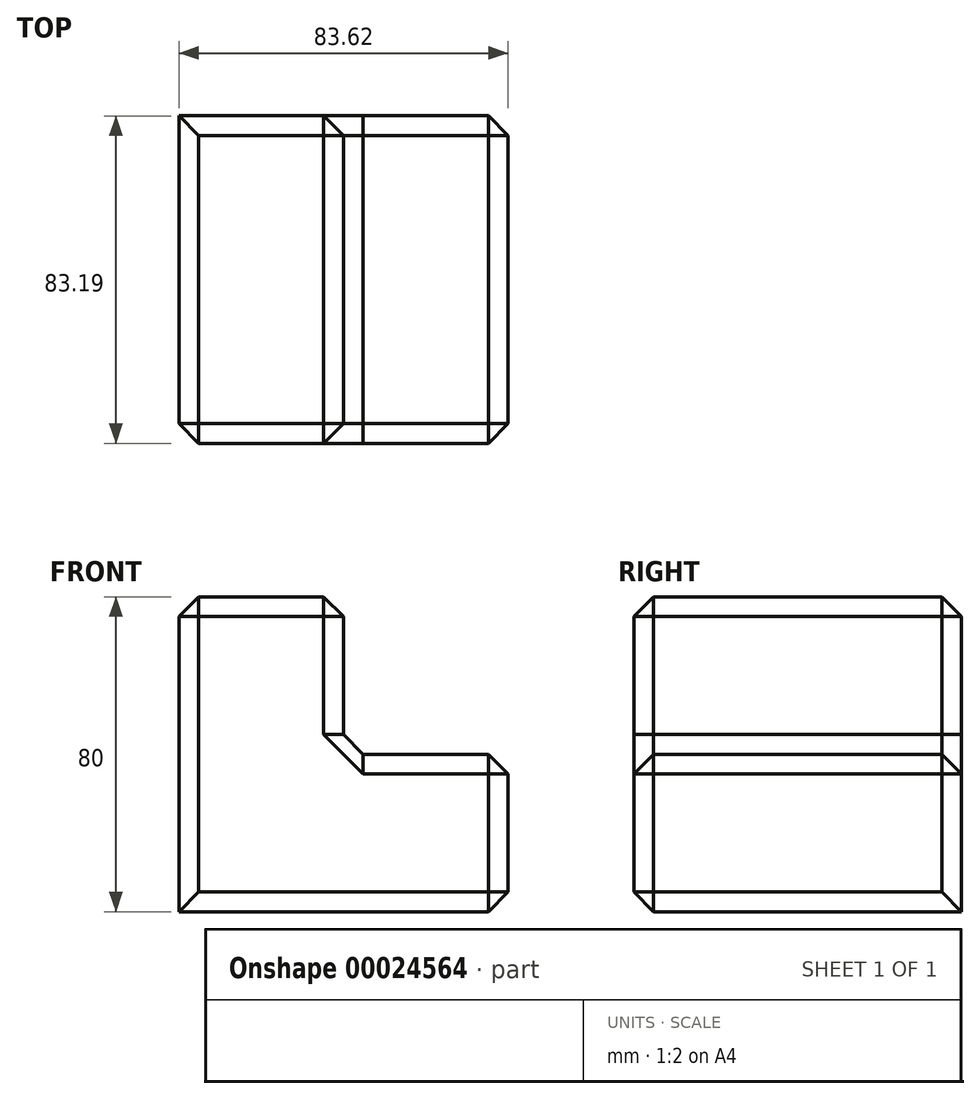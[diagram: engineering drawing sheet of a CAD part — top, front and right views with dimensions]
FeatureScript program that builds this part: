
annotation { "Feature Type Name" : "Feature", "Feature Type Description" : "" }
export const myFeature = defineFeature(function(context is Context, id is Id, definition is map)
    precondition{}
    {
        {
            var Q0;
            Q0=qCreatedBy(makeId("Top.planeOp"),FACE);
            var sketch = newSketch(context, id + "F0", { "sketchPlane" : qUnion([Q0])});
            skLineSegment(sketch, "E0.bottom", {"start": v(-59.13, -45.93) * mm, "end": v(24.5, -45.93) * mm});
            skLineSegment(sketch, "E0.top", {"start": v(-59.13, 37.26) * mm, "end": v(24.5, 37.26) * mm});
            skLineSegment(sketch, "E0.left", {"start": v(-59.13, -45.93) * mm, "end": v(-59.13, 37.26) * mm});
            skLineSegment(sketch, "E0.right", {"start": v(24.5, -45.93) * mm, "end": v(24.5, 37.26) * mm});
            skSolve(sketch);
        }
        {
            var Q0;
            Q0=makeQuery(id+"F0.imprint","IMPRINT",FACE,{"disambiguationData":[TD([[makeQuery(id+"F0.imprint","IMPRINT",EDGE,{"derivedFrom":sQuery(id+"F0.wireOp",EDGE,"E0.bottom")}),1.0]])]});
            extrude(context, id + "F1", {"entities" : qUnion([Q0]), "depth" : 40 * mm});
        }
        {
            var Q0;
            Q0=makeQuery(id+"F1.opExtrude","CAP_FACE",FACE,{"disambiguationData":[OSD([sQuery(id+"F0.wireOp",EDGE,"E0.bottom"),sQuery(id+"F0.wireOp",EDGE,"E0.top"),sQuery(id+"F0.wireOp",EDGE,"E0.left"),sQuery(id+"F0.wireOp",EDGE,"E0.right")])],"isStart":false});
            var sketch = newSketch(context, id + "F2", { "sketchPlane" : qUnion([Q0])});
            skLineSegment(sketch, "E1", {"start": v(-17.32, 37.26) * mm, "end": v(-17.32, -45.93) * mm});
            skSolve(sketch);
        }
        {
            var Q0;
            {var subQ1=sQuery(id+"F2.wireOp",EDGE,"E1");Q0=makeQuery(id+"F2.imprint","IMPRINT",FACE,{"disambiguationData":[TD([[makeQuery(id+"F2.imprint","IMPRINT",EDGE,{"derivedFrom":subQ1}),-1.0]])]});}
            extrude(context, id + "F3", {"entities" : qUnion([Q0]), "operationType" : NewBodyOperationType.ADD, "depth" : 40 * mm});
        }
        {
            var Q0;
            Q0=makeQuery(id+"F3.opExtrude","CAP_FACE",FACE,{"disambiguationData":[OSD([sQuery(id+"F0.wireOp",EDGE,"E0.bottom"),sQuery(id+"F0.wireOp",EDGE,"E0.top"),sQuery(id+"F0.wireOp",EDGE,"E0.left"),sQuery(id+"F2.wireOp",EDGE,"E1")])],"isStart":false});
            var Q1;
            {var subQ0=sQuery(id+"F0.wireOp",EDGE,"E0.bottom");Q1=makeQuery(id+"F3.boolean.opBoolean","MERGE",FACE,{"derivedFrom":[makeQuery(id+"F1.opExtrude","SWEPT_FACE",FACE,{"disambiguationData":[OSD([subQ0])]}),makeQuery(id+"F3.opExtrude","SWEPT_FACE",FACE,{"disambiguationData":[OSD([subQ0])]})]});}
            var Q2;
            Q2=makeQuery(id+"F1.opExtrude","CAP_FACE",FACE,{"disambiguationData":[OSD([sQuery(id+"F0.wireOp",EDGE,"E0.bottom"),sQuery(id+"F0.wireOp",EDGE,"E0.top"),sQuery(id+"F0.wireOp",EDGE,"E0.left"),sQuery(id+"F0.wireOp",EDGE,"E0.right")])],"isStart":false});
            var Q3;
            Q3=makeQuery(id+"F3.opExtrude","SWEPT_FACE",FACE,{"disambiguationData":[OSD([sQuery(id+"F2.wireOp",EDGE,"E1")])]});
            var Q4;
            Q4=makeQuery(id+"F1.opExtrude","SWEPT_FACE",FACE,{"disambiguationData":[OSD([sQuery(id+"F0.wireOp",EDGE,"E0.right")])]});
            chamfer(context, id + "F4", {"entities" : qUnion([Q0, Q1, Q2, Q3, Q4]), "width" : 5 * mm, "tangentPropagation" : true});
        }
    });
